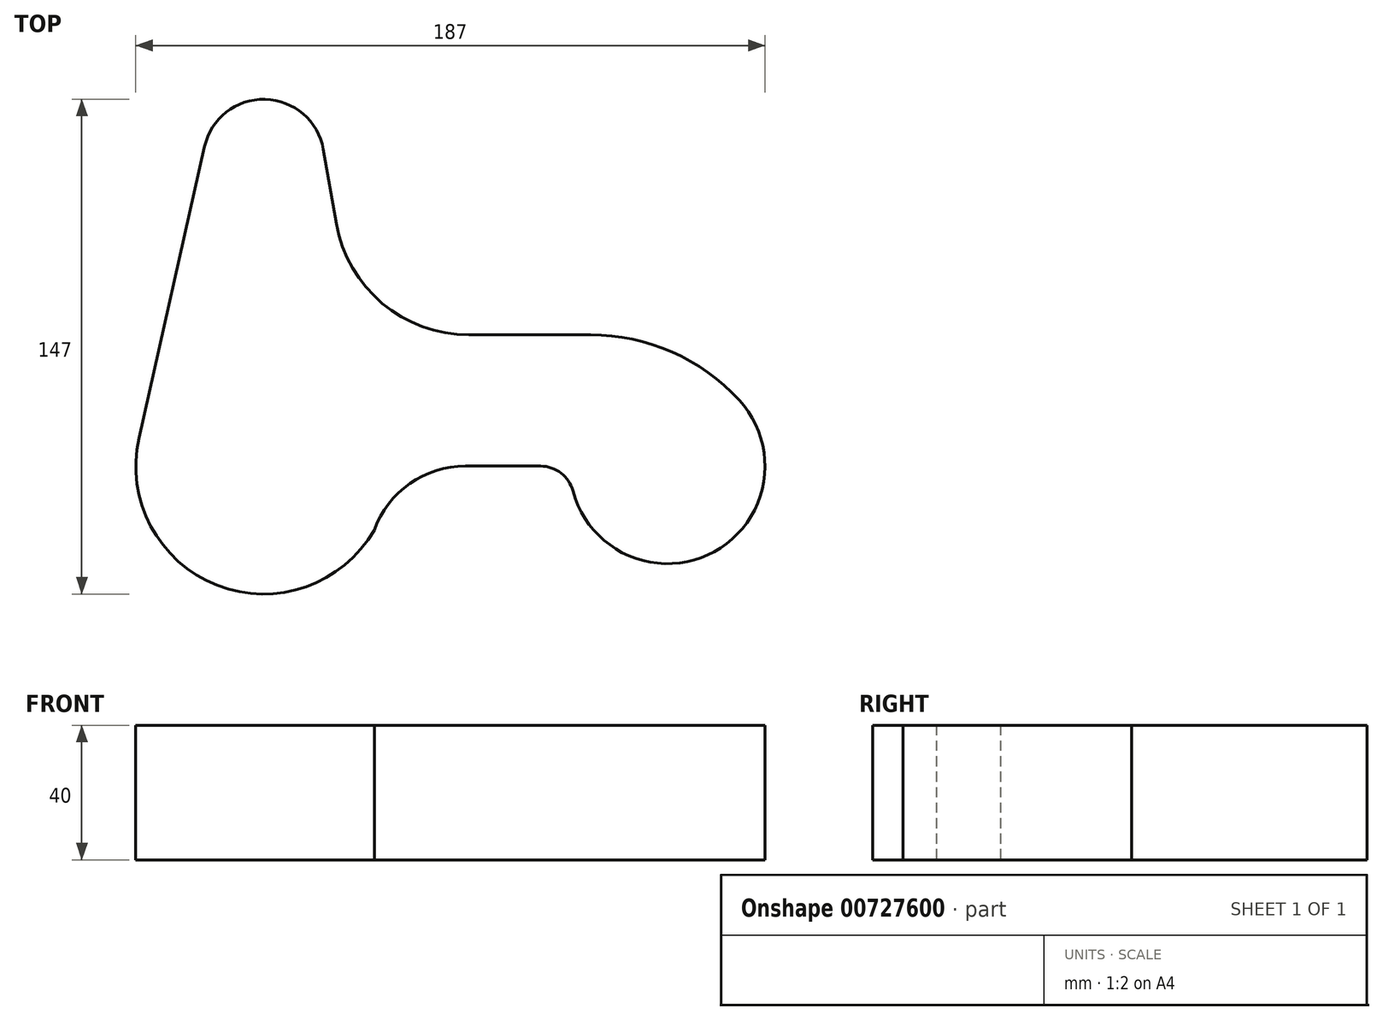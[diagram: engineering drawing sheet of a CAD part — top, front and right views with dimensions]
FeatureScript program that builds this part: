
annotation { "Feature Type Name" : "Feature", "Feature Type Description" : "" }
export const myFeature = defineFeature(function(context is Context, id is Id, definition is map)
    precondition{}
    {
        {
            var Q0;
            Q0=qCreatedBy(makeId("Top.planeOp"),FACE);
            var sketch = newSketch(context, id + "F0", { "sketchPlane" : qUnion([Q0])});
            skLineSegment(sketch, "E0", {"start": v(0, 0) * mm, "end": v(38, 0) * mm, "construction": true});
            skLineSegment(sketch, "E1", {"start": v(0, 0) * mm, "end": v(0, 91) * mm, "construction": true});
            skLineSegment(sketch, "E2", {"start": v(0, 91) * mm, "end": v(-7, 91) * mm, "construction": true});
            skArc(sketch, "E3", {"start": v(-37.07, 8.35) * mm, "mid": v(-13.83, -35.4) * mm, "end": v(32.9, -19) * mm});
            skArc(sketch, "E4", {"start": v(17.73, 94.12) * mm, "mid": v(0.43, 109) * mm, "end": v(-17.56, 94.96) * mm});
            skArc(sketch, "E5", {"start": v(91.97, -7.44) * mm, "mid": v(133.95, -25.43) * mm, "end": v(141.33, 19.65) * mm});
            skArc(sketch, "E6", {"start": v(21.6, 72.07) * mm, "mid": v(35.28, 48.36) * mm, "end": v(61, 39) * mm});
            skLineSegment(sketch, "E7", {"start": v(17.73, 94.12) * mm, "end": v(21.6, 72.07) * mm});
            skArc(sketch, "E8", {"start": v(141.33, 19.65) * mm, "mid": v(121.3, 33.95) * mm, "end": v(97.2, 39) * mm});
            skArc(sketch, "E9", {"start": v(91.97, -7.44) * mm, "mid": v(88.4, -2.07) * mm, "end": v(82.3, 0) * mm});
            skLineSegment(sketch, "E10", {"start": v(61, 39) * mm, "end": v(97.2, 39) * mm});
            skLineSegment(sketch, "E11", {"start": v(0, 0) * mm, "end": v(54.5, -31.46) * mm, "construction": true});
            skLineSegment(sketch, "E12", {"start": v(-37.07, 8.35) * mm, "end": v(-17.56, 94.96) * mm});
            skLineSegment(sketch, "E13", {"start": v(60, 0) * mm, "end": v(82.3, 0) * mm});
            skArc(sketch, "E14", {"start": v(60, 0) * mm, "mid": v(43.46, -5.22) * mm, "end": v(32.9, -19) * mm});
            skSolve(sketch);
        }
        {
            var Q0;
            Q0=makeQuery(id+"F0.imprint","IMPRINT",FACE,{"disambiguationData":[TD([[makeQuery(id+"F0.imprint","IMPRINT",EDGE,{"derivedFrom":sQuery(id+"F0.wireOp",EDGE,"E3")}),1.0]])]});
            extrude(context, id + "F1", {"entities" : qUnion([Q0]), "depth" : 40 * mm, "offsetDistance" : 25.4 * mm});
        }
    });
